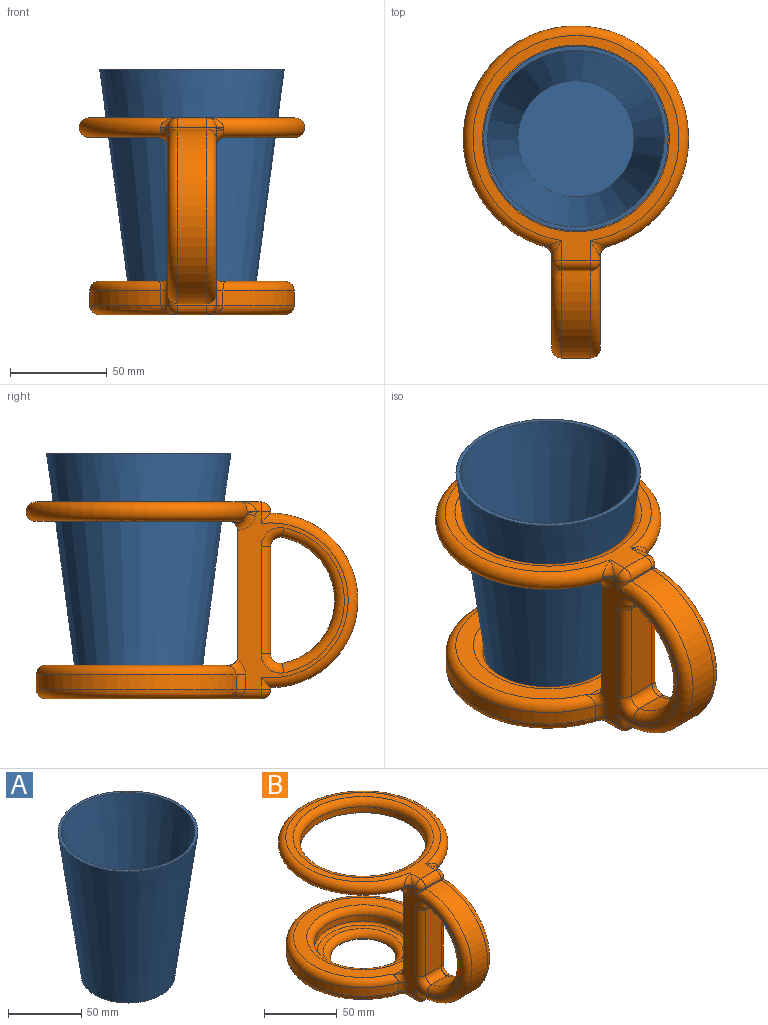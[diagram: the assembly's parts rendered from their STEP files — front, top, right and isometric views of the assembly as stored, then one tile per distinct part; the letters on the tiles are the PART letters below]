
ASSEMBLY  parts=2 mates=1
PART A: 5 faces, bbox 95.3x95.3x120.7 mm
  f0: plane 63.5x63.5mm, normal (0,0,-1), area 3166.9mm2, adj f2
  f1: plane 95.25x95.25mm, normal (0,0,1), area 590.8mm2, adj f2,f4
  f2: cone r=31.75mm half-angle=7.5deg, axis (0,0,1), area 30345.1mm2, adj f0,f1
  f3: plane 59.99x59.99mm, normal (0,0,1), area 2826.7mm2, adj f4
  f4: cone r=29.77mm half-angle=7.5deg, axis (0,0,1), area 28424.2mm2, adj f1,f3
PART B: 68 faces, bbox 126x179.9x101.6 mm
  f0: plane 55.1x15mm, normal (0,-1,0), area 826.5mm2, adj f39,f42,f44,f47
  f1: plane 15x0.8mm, normal (0,-1,0), area 12mm2, adj f12,f16,f31,f36
  f2: cylinder r=43.18mm len=86.36mm, axis (0,0,-1), area 1356.5mm2, adj f4,f5
  f3: plane 116.36x106.36mm, normal (0,0,1), area 1744.8mm2, adj f5,f13,f14,f15,f16
  f4: plane 106.36x103.43mm, normal (0,0,-1), area 2820.7mm2, adj f2,f13,f53,f54,f57
  f5: torus R=48.18mm, axis (0,0,1), area 2220.5mm2, adj f2,f3
  f6: plane 91.6x57.33mm, normal (1,0,0), area 1286.8mm2, adj f8,f14,f24,f34,f35,f36,f43,f45
  f7: plane 91.6x57.33mm, normal (-1,0,0), area 1286.8mm2, adj f8,f15,f23,f29,f30,f31,f38,f39
  f8: plane 64.3x25mm, normal (0,1,0), area 1607.5mm2, adj f6,f7,f53,f67
  f9: plane 15x0.8mm, normal (0,-1,0), area 12mm2, adj f12,f22,f29,f34
  f10: plane 110.96x95.56mm, normal (0,0,-1), area 5816mm2, adj f22,f23,f24,f25,f49
  f11: cylinder r=33mm len=64.94mm, axis (-1,0,0), area 1377.3mm2, adj f38,f42,f43,f44
  f12: cylinder r=45mm len=90mm, axis (-1,0,0), area 2120.6mm2, adj f1,f9,f30,f35
  f13: torus R=53.18mm, axis (0,0,1), area 5087.5mm2, adj f3,f4,f26,f27,f51,f52,f55,f59
  f14: cylinder r=5mm len=10.53mm, axis (0,-1,0), area 41.8mm2, adj f3,f6,f26,f37
  f15: cylinder r=5mm len=10.53mm, axis (0,1,0), area 41.8mm2, adj f3,f7,f27,f32
  f16: cylinder r=5mm len=15mm, axis (1,0,0), area 117.8mm2, adj f1,f3,f32,f37
  f17: cylinder r=52.78mm len=105.56mm, axis (0,0,1), area 2183.8mm2, adj f25,f60,f62,f65
  f18: plane 95.61x94.11mm, normal (0,0,1), area 2461mm2, adj f21,f60,f61,f64,f67
  f19: cylinder r=33.65mm len=67.31mm, axis (0,0,1), area 1057.3mm2, adj f21,f48
  f20: plane 63.31x63.31mm, normal (0,0,1), area 772.2mm2, adj f48,f50
  f21: torus R=38.66mm, axis (0,0,-1), area 1750.5mm2, adj f18,f19
  f22: cylinder r=5mm len=15mm, axis (1,0,0), area 117.8mm2, adj f9,f10,f28,f33
  f23: cylinder r=5mm len=15.99mm, axis (0,1,0), area 94.7mm2, adj f7,f10,f28,f66
  f24: cylinder r=5mm len=15.99mm, axis (0,-1,0), area 94.7mm2, adj f6,f10,f33,f63
  f25: torus R=47.78mm, axis (0,0,-1), area 2327.7mm2, adj f10,f17,f63,f66
  f26: bspline ~8.62x8.07mm, area 22.5mm2, adj f13,f14,f52
  f27: bspline ~8.62x8.07mm, area 22.5mm2, adj f13,f15,f51
  f28: sphere r=5mm, area 39.3mm2, adj f22,f23,f29
  f29: cylinder r=5mm len=6.11mm, axis (0,0,-1), area 21.1mm2, adj f7,f9,f28,f30
  f30: torus R=40mm, axis (1,0,0), area 1107.2mm2, adj f7,f12,f29,f31
  f31: cylinder r=5mm len=6.11mm, axis (0,0,-1), area 21.1mm2, adj f1,f7,f30,f32
  f32: sphere r=5mm, area 39.3mm2, adj f15,f16,f31
  f33: sphere r=5mm, area 39.3mm2, adj f22,f24,f34
  f34: cylinder r=5mm len=6.11mm, axis (0,0,1), area 21.1mm2, adj f6,f9,f33,f35
  f35: torus R=40mm, axis (1,0,0), area 1107.2mm2, adj f6,f12,f34,f36
  f36: cylinder r=5mm len=6.11mm, axis (0,0,1), area 21.1mm2, adj f1,f6,f35,f37
  f37: sphere r=5mm, area 39.3mm2, adj f14,f16,f36
  f38: torus R=38mm, axis (1,0,0), area 760.9mm2, adj f7,f11,f40,f41
  f39: cylinder r=5mm len=55.1mm, axis (0,0,-1), area 432.8mm2, adj f0,f7,f40,f41
  f40: torus R=10mm, axis (1,0,0), area 93.7mm2, adj f7,f38,f39,f42
  f41: torus R=10mm, axis (1,0,0), area 93.7mm2, adj f7,f38,f39,f44
  f42: cylinder r=5mm len=15mm, axis (-1,0,0), area 131.3mm2, adj f0,f11,f40,f45
  f43: torus R=38mm, axis (1,0,0), area 760.9mm2, adj f6,f11,f45,f46
  f44: cylinder r=5mm len=15mm, axis (-1,0,0), area 131.3mm2, adj f0,f11,f41,f46
  f45: torus R=10mm, axis (1,0,0), area 93.7mm2, adj f6,f42,f43,f47
  f46: torus R=10mm, axis (1,0,0), area 93.7mm2, adj f6,f43,f44,f47
  f47: cylinder r=5mm len=55.1mm, axis (0,0,1), area 432.8mm2, adj f0,f6,f45,f46
  f48: torus R=31.66mm, axis (0,0,-1), area 650mm2, adj f19,f20
  f49: cylinder r=22.5mm len=45mm, axis (0,0,1), area 42.4mm2, adj f10,f50
  f50: torus R=27.5mm, axis (0,0,-1), area 1200mm2, adj f20,f49
  f51: torus R=10mm, axis (0,0,1), area 2.7mm2, adj f13,f27,f56
  f52: torus R=10mm, axis (0,0,1), area 2.7mm2, adj f13,f26,f58
  f53: cylinder r=5mm len=34.8mm, axis (-1,0,0), area 224mm2, adj f4,f6,f7,f8,f54,f55,f57,f59
  f54: cylinder r=4.9mm len=3.97mm, axis (0,-1,0), area 9mm2, adj f4,f53,f55
  f55: bspline ~11.36x9.37mm, area 66mm2, adj f7,f13,f53,f54,f56
  f56: bspline ~5x3.76mm, area 7.7mm2, adj f7,f51,f55
  f57: cylinder r=4.9mm len=3.97mm, axis (0,1,0), area 9mm2, adj f4,f53,f59
  f58: bspline ~5x3.76mm, area 7.7mm2, adj f6,f52,f59
  f59: bspline ~12.57x9.38mm, area 66mm2, adj f6,f13,f53,f57,f58
  f60: torus R=47.78mm, axis (0,0,-1), area 2242.2mm2, adj f17,f18,f61,f64
  f61: bspline ~11.63x11.26mm, area 54.2mm2, adj f6,f18,f60,f62,f67
  f62: cylinder r=5mm len=7.3mm, axis (0,0,1), area 46.1mm2, adj f6,f17,f61,f63
  f63: bspline ~8.49x7.88mm, area 22mm2, adj f24,f25,f62
  f64: bspline ~11.63x11.26mm, area 54.2mm2, adj f7,f18,f60,f65,f67
  f65: cylinder r=5mm len=7.3mm, axis (0,0,1), area 46.1mm2, adj f7,f17,f64,f66
  f66: bspline ~8.49x7.88mm, area 22mm2, adj f23,f25,f65
  f67: cylinder r=5mm len=31.86mm, axis (1,0,0), area 216.2mm2, adj f6,f7,f8,f18,f61,f64
PLACE A rot(axis=(0,0,-1),12.6deg) t=(85.56,55.97,-141.25)mm
PLACE B t=(85.56,55.97,-55.76)mm fixed
MATE cylindrical B.f2 <-> A.f2  axis (0,0,1) through (85.56,55.97,-50.76)mm
